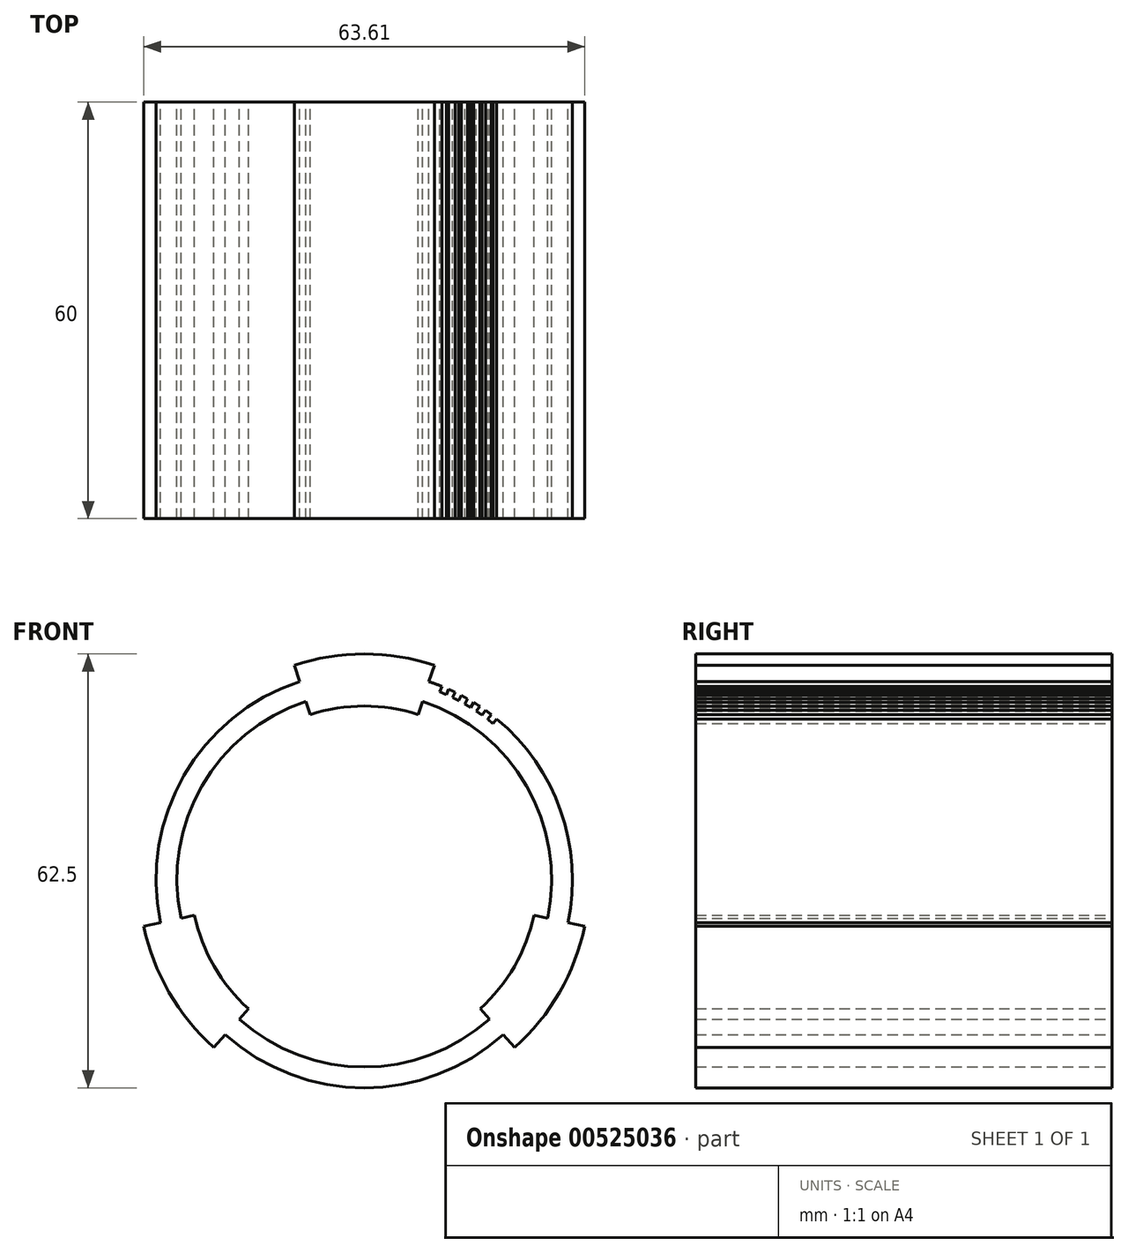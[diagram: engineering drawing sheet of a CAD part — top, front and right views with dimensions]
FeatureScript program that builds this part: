
annotation { "Feature Type Name" : "Feature", "Feature Type Description" : "" }
export const myFeature = defineFeature(function(context is Context, id is Id, definition is map)
    precondition{}
    {
        {
            var Q0;
            Q0=qCreatedBy(makeId("Front.planeOp"),FACE);
            var sketch = newSketch(context, id + "F0", { "sketchPlane" : qUnion([Q0])});
            skArc(sketch, "E0", {"start": v(-14.55, 20.43) * mm, "mid": v(-31.2, 6.92) * mm, "end": v(-34.58, -14.27) * mm});
            skArc(sketch, "E1.0", {"start": v(-13.61, 17.58) * mm, "mid": v(-28.6, 5.42) * mm, "end": v(-31.64, -13.65) * mm});
            skLineSegment(sketch, "E2", {"start": v(-13, 15.68) * mm, "end": v(-13.61, 17.58) * mm});
            skLineSegment(sketch, "E3.MirrorCS", {"start": v(2.54, 15.68) * mm, "end": v(3.17, 17.58) * mm});
            skArc(sketch, "E4.trimOffspring", {"start": v(4.87, 22.8) * mm, "mid": v(-5.22, 24.42) * mm, "end": v(-15.32, 22.8) * mm});
            skArc(sketch, "E5.trimOffspring", {"start": v(2.54, 15.68) * mm, "mid": v(-5.22, 16.92) * mm, "end": v(-13, 15.68) * mm});
            skPoint(sketch, "E6.start.orphan", {"position": v(-15.32, -38.97) * mm});
            skPoint(sketch, "E7.trimOffspring.end.orphan", {"position": v(4.87, -38.97) * mm});
            skLineSegment(sketch, "E8.trimOffspring", {"start": v(-14.55, 20.43) * mm, "end": v(-15.32, 22.8) * mm});
            skLineSegment(sketch, "E9.trimOffspring", {"start": v(4.1, 20.43) * mm, "end": v(4.87, 22.8) * mm});
            skLineSegment(sketch, "E10", {"start": v(-5.22, -8.08) * mm, "end": v(-5.22, 24.42) * mm});
            skArc(sketch, "E11.1.0", {"start": v(-37.03, -14.78) * mm, "mid": v(-33.37, -24.33) * mm, "end": v(-26.93, -32.27) * mm});
            skArc(sketch, "E11.1.1", {"start": v(-29.69, -13.23) * mm, "mid": v(-26.88, -20.58) * mm, "end": v(-21.92, -26.7) * mm});
            skLineSegment(sketch, "E11.1.2", {"start": v(-25.26, -30.41) * mm, "end": v(-26.93, -32.27) * mm});
            skLineSegment(sketch, "E11.1.3", {"start": v(-21.92, -26.7) * mm, "end": v(-23.25, -28.18) * mm});
            skLineSegment(sketch, "E11.1.4", {"start": v(-29.69, -13.23) * mm, "end": v(-31.64, -13.65) * mm});
            skLineSegment(sketch, "E11.1.5", {"start": v(-34.58, -14.27) * mm, "end": v(-37.03, -14.78) * mm});
            skArc(sketch, "E11.2.0", {"start": v(16.48, -32.27) * mm, "mid": v(22.92, -24.33) * mm, "end": v(26.58, -14.78) * mm});
            skArc(sketch, "E11.2.1", {"start": v(11.47, -26.7) * mm, "mid": v(16.43, -20.58) * mm, "end": v(19.24, -13.23) * mm});
            skLineSegment(sketch, "E11.2.2", {"start": v(24.13, -14.27) * mm, "end": v(26.58, -14.78) * mm});
            skLineSegment(sketch, "E11.2.3", {"start": v(19.24, -13.23) * mm, "end": v(21.2, -13.65) * mm});
            skLineSegment(sketch, "E11.2.4", {"start": v(11.47, -26.7) * mm, "end": v(12.8, -28.18) * mm});
            skLineSegment(sketch, "E11.2.5", {"start": v(14.8, -30.41) * mm, "end": v(16.48, -32.27) * mm});
            skArc(sketch, "E12.trimOffspring", {"start": v(21.2, -13.65) * mm, "mid": v(18.16, 5.42) * mm, "end": v(3.17, 17.58) * mm});
            skArc(sketch, "E13.trimOffspring", {"start": v(24.13, -14.27) * mm, "mid": v(23.1, 1.83) * mm, "end": v(13.87, 15.06) * mm});
            skArc(sketch, "E14.trimOffspring", {"start": v(-23.25, -28.18) * mm, "mid": v(-5.22, -35.08) * mm, "end": v(12.8, -28.18) * mm});
            skArc(sketch, "E15.trimOffspring", {"start": v(-25.26, -30.41) * mm, "mid": v(-5.22, -38.08) * mm, "end": v(14.8, -30.41) * mm});
            skLineSegment(sketch, "E16", {"start": v(5.68, 18.96) * mm, "end": v(6, 19.74) * mm});
            skLineSegment(sketch, "E17.1.0", {"start": v(6.6, 18.57) * mm, "end": v(6.94, 19.34) * mm});
            skLineSegment(sketch, "E17.2.0", {"start": v(7.5, 18.15) * mm, "end": v(7.86, 18.91) * mm});
            skLineSegment(sketch, "E17.3.0", {"start": v(8.38, 17.7) * mm, "end": v(8.77, 18.45) * mm});
            skLineSegment(sketch, "E17.4.0", {"start": v(9.25, 17.22) * mm, "end": v(9.67, 17.96) * mm});
            skLineSegment(sketch, "E17.5.0", {"start": v(10.1, 16.72) * mm, "end": v(10.55, 17.44) * mm});
            skLineSegment(sketch, "E17.6.0", {"start": v(10.94, 16.18) * mm, "end": v(11.4, 16.89) * mm});
            skLineSegment(sketch, "E17.7.0", {"start": v(11.75, 15.62) * mm, "end": v(12.25, 16.3) * mm});
            skLineSegment(sketch, "E17.8.0", {"start": v(12.55, 15.02) * mm, "end": v(13.07, 15.7) * mm});
            skLineSegment(sketch, "E17.9.0", {"start": v(13.33, 14.4) * mm, "end": v(13.87, 15.06) * mm});
            skLineSegment(sketch, "E17.anchor1", {"start": v(5.68, 18.96) * mm, "end": v(6, 19.74) * mm, "construction": true});
            skLineSegment(sketch, "E17.anchor2", {"start": v(13.33, 14.4) * mm, "end": v(13.87, 15.06) * mm, "construction": true});
            skArc(sketch, "E18", {"start": v(13.33, 14.4) * mm, "mid": v(12.94, 14.72) * mm, "end": v(12.55, 15.02) * mm});
            skArc(sketch, "E19.trimOffspring", {"start": v(6.6, 18.57) * mm, "mid": v(6.14, 18.77) * mm, "end": v(5.68, 18.96) * mm});
            skArc(sketch, "E20.trimOffspring", {"start": v(8.38, 17.7) * mm, "mid": v(7.94, 17.93) * mm, "end": v(7.5, 18.15) * mm});
            skArc(sketch, "E21.trimOffspring", {"start": v(10.1, 16.72) * mm, "mid": v(9.68, 16.97) * mm, "end": v(9.25, 17.22) * mm});
            skArc(sketch, "E22.trimOffspring", {"start": v(11.75, 15.62) * mm, "mid": v(11.35, 15.9) * mm, "end": v(10.94, 16.18) * mm});
            skArc(sketch, "E23.trimOffspring", {"start": v(6, 19.74) * mm, "mid": v(5.05, 20.1) * mm, "end": v(4.1, 20.43) * mm});
            skArc(sketch, "E24.trimOffspring", {"start": v(7.86, 18.91) * mm, "mid": v(7.4, 19.13) * mm, "end": v(6.94, 19.34) * mm});
            skArc(sketch, "E25.trimOffspring", {"start": v(9.67, 17.96) * mm, "mid": v(9.22, 18.21) * mm, "end": v(8.77, 18.45) * mm});
            skArc(sketch, "E26.trimOffspring", {"start": v(11.4, 16.89) * mm, "mid": v(10.98, 17.17) * mm, "end": v(10.55, 17.44) * mm});
            skArc(sketch, "E27.trimOffspring", {"start": v(13.07, 15.7) * mm, "mid": v(12.66, 16) * mm, "end": v(12.25, 16.3) * mm});
            skSolve(sketch);
        }
        {
            var Q0;
            Q0=makeQuery(id+"F0.imprint","IMPRINT",FACE,{"disambiguationData":[TD([[makeQuery(id+"F0.imprint","IMPRINT",EDGE,{"derivedFrom":sQuery(id+"F0.wireOp",EDGE,"E0")}),1.0]])]});
            extrude(context, id + "F1", {"entities" : qUnion([Q0]), "depth" : 60 * mm, "offsetDistance" : 25 * mm});
        }
    });
